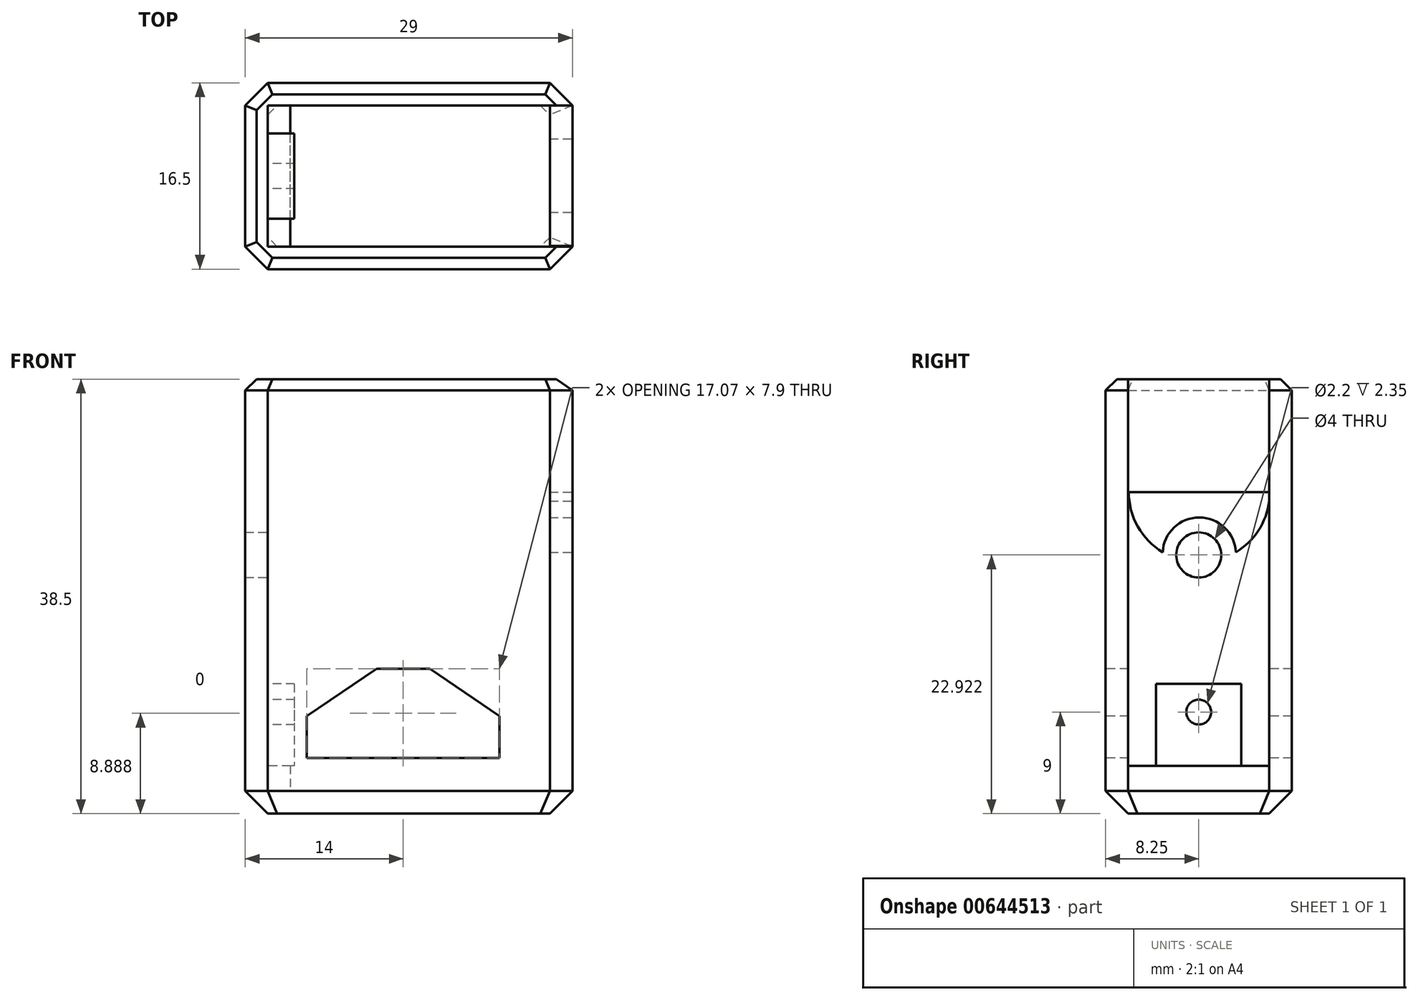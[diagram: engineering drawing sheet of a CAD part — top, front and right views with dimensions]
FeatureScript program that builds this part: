
annotation { "Feature Type Name" : "Feature", "Feature Type Description" : "" }
export const myFeature = defineFeature(function(context is Context, id is Id, definition is map)
    precondition{}
    {
        {
            var Q0;
            Q0=qCreatedBy(makeId("Top.planeOp"),FACE);
            var sketch = newSketch(context, id + "F0", { "sketchPlane" : qUnion([Q0])});
            skLineSegment(sketch, "E0.bottom", {"start": v(0, 0) * mm, "end": v(29, 0) * mm});
            skLineSegment(sketch, "E0.top", {"start": v(0, 16.5) * mm, "end": v(29, 16.5) * mm});
            skLineSegment(sketch, "E0.left", {"start": v(0, 0) * mm, "end": v(0, 16.5) * mm});
            skLineSegment(sketch, "E0.right", {"start": v(29, 0) * mm, "end": v(29, 16.5) * mm});
            skSolve(sketch);
        }
        {
            var Q0;
            Q0=makeQuery(id+"F0.imprint","IMPRINT",FACE,{"disambiguationData":[TD([[makeQuery(id+"F0.imprint","IMPRINT",EDGE,{"derivedFrom":sQuery(id+"F0.wireOp",EDGE,"E0.bottom")}),1.0]])]});
            extrude(context, id + "F1", {"entities" : qUnion([Q0]), "depth" : 38.5 * mm, "offsetDistance" : 25 * mm});
        }
        {
            var Q0;
            Q0=makeQuery(id+"F1.opExtrude","SWEPT_EDGE",EDGE,{"disambiguationData":[OSD([sQuery(id+"F0.wireOp",EDGE,"E0.bottom"),sQuery(id+"F0.wireOp",EDGE,"E0.left")])]});
            var Q1;
            Q1=makeQuery(id+"F1.opExtrude","SWEPT_EDGE",EDGE,{"disambiguationData":[OSD([sQuery(id+"F0.wireOp",EDGE,"E0.top"),sQuery(id+"F0.wireOp",EDGE,"E0.left")])]});
            var Q2;
            Q2=makeQuery(id+"F1.opExtrude","SWEPT_EDGE",EDGE,{"disambiguationData":[OSD([sQuery(id+"F0.wireOp",EDGE,"E0.bottom"),sQuery(id+"F0.wireOp",EDGE,"E0.right")])]});
            var Q3;
            Q3=makeQuery(id+"F1.opExtrude","SWEPT_EDGE",EDGE,{"disambiguationData":[OSD([sQuery(id+"F0.wireOp",EDGE,"E0.top"),sQuery(id+"F0.wireOp",EDGE,"E0.right")])]});
            chamfer(context, id + "F2", {"entities" : qUnion([Q0, Q1, Q2, Q3]), "width" : 2 * mm, "tangentPropagation" : true});
        }
        {
            var Q0;
            Q0=makeQuery(id+"F1.opExtrude","CAP_FACE",FACE,{"disambiguationData":[OSD([sQuery(id+"F0.wireOp",EDGE,"E0.bottom"),sQuery(id+"F0.wireOp",EDGE,"E0.top"),sQuery(id+"F0.wireOp",EDGE,"E0.left"),sQuery(id+"F0.wireOp",EDGE,"E0.right")])],"isStart":true});
            chamfer(context, id + "F3", {"entities" : qUnion([Q0]), "width" : 2 * mm, "tangentPropagation" : true});
        }
        {
            var Q0;
            Q0=makeQuery(id+"F1.opExtrude","CAP_FACE",FACE,{"disambiguationData":[OSD([sQuery(id+"F0.wireOp",EDGE,"E0.bottom"),sQuery(id+"F0.wireOp",EDGE,"E0.top"),sQuery(id+"F0.wireOp",EDGE,"E0.left"),sQuery(id+"F0.wireOp",EDGE,"E0.right")])],"isStart":false});
            chamfer(context, id + "F4", {"entities" : qUnion([Q0]), "width" : 1 * mm, "tangentPropagation" : true});
        }
        {
            var Q0;
            Q0=makeQuery(id+"F1.opExtrude","CAP_FACE",FACE,{"disambiguationData":[OSD([sQuery(id+"F0.wireOp",EDGE,"E0.bottom"),sQuery(id+"F0.wireOp",EDGE,"E0.top"),sQuery(id+"F0.wireOp",EDGE,"E0.left"),sQuery(id+"F0.wireOp",EDGE,"E0.right")])],"isStart":false});
            var sketch = newSketch(context, id + "F5", { "sketchPlane" : qUnion([Q0])});
            skLineSegment(sketch, "E1.bottom", {"start": v(2, 2) * mm, "end": v(27, 2) * mm});
            skLineSegment(sketch, "E1.top", {"start": v(2, 14.5) * mm, "end": v(27, 14.5) * mm});
            skLineSegment(sketch, "E1.left", {"start": v(2, 2) * mm, "end": v(2, 14.5) * mm});
            skLineSegment(sketch, "E1.right", {"start": v(27, 2) * mm, "end": v(27, 14.5) * mm});
            skSolve(sketch);
        }
        {
            var Q0;
            Q0=makeQuery(id+"F5.imprint","IMPRINT",FACE,{"disambiguationData":[TD([[makeQuery(id+"F5.imprint","IMPRINT",EDGE,{"derivedFrom":sQuery(id+"F5.wireOp",EDGE,"E1.bottom")}),1.0]])]});
            extrude(context, id + "F6", {"entities" : qUnion([Q0]), "operationType" : NewBodyOperationType.REMOVE, "oppositeDirection" : true, "depth" : 34.25 * mm, "offsetDistance" : 25 * mm});
        }
        {
            var Q0;
            Q0=makeQuery(id+"F1.opExtrude","SWEPT_FACE",FACE,{"disambiguationData":[OSD([sQuery(id+"F0.wireOp",EDGE,"E0.bottom")])]});
            var sketch = newSketch(context, id + "F7", { "sketchPlane" : qUnion([Q0])});
            skLineSegment(sketch, "E2", {"start": v(5.46, 4.94) * mm, "end": v(22.54, 4.94) * mm});
            skLineSegment(sketch, "E3", {"start": v(22.54, 4.94) * mm, "end": v(22.54, 8.66) * mm});
            skLineSegment(sketch, "E4", {"start": v(22.54, 8.66) * mm, "end": v(16.36, 12.84) * mm});
            skLineSegment(sketch, "E5", {"start": v(16.36, 12.84) * mm, "end": v(11.64, 12.84) * mm});
            skLineSegment(sketch, "E6", {"start": v(11.64, 12.84) * mm, "end": v(5.46, 8.66) * mm});
            skLineSegment(sketch, "E7", {"start": v(5.46, 8.66) * mm, "end": v(5.46, 4.94) * mm});
            skSolve(sketch);
        }
        {
            var Q0;
            Q0=makeQuery(id+"F7.imprint","IMPRINT",FACE,{"disambiguationData":[TD([[makeQuery(id+"F7.imprint","IMPRINT",EDGE,{"derivedFrom":sQuery(id+"F7.wireOp",EDGE,"E2")}),1.0]])]});
            extrude(context, id + "F8", {"entities" : qUnion([Q0]), "operationType" : NewBodyOperationType.REMOVE, "endBound" : BoundingType.THROUGH_ALL, "oppositeDirection" : true, "depth" : 25 * mm, "offsetDistance" : 25 * mm});
        }
        {
            var Q0;
            Q0=makeQuery(id+"F1.opExtrude","SWEPT_FACE",FACE,{"disambiguationData":[OSD([sQuery(id+"F0.wireOp",EDGE,"E0.right")])]});
            var sketch = newSketch(context, id + "F9", { "sketchPlane" : qUnion([Q0])});
            skCircle(sketch, "E8", {"center": v(8.3, 23) * mm, "radius": 3.25 * mm});
            skCircle(sketch, "E9", {"center": v(8.3, 28.5) * mm, "radius": 6.25 * mm});
            skLineSegment(sketch, "E10.bottom", {"start": v(2, 38.5) * mm, "end": v(14.5, 38.5) * mm});
            skLineSegment(sketch, "E10.top", {"start": v(2, 28.5) * mm, "end": v(14.5, 28.5) * mm});
            skLineSegment(sketch, "E10.left", {"start": v(2, 38.5) * mm, "end": v(2, 28.5) * mm});
            skLineSegment(sketch, "E10.right", {"start": v(14.5, 38.5) * mm, "end": v(14.5, 28.5) * mm});
            skSolve(sketch);
        }
        {
            var Q0;
            {var subQ0=sQuery(id+"F9.wireOp",EDGE,"E10.bottom");Q0=makeQuery(id+"F9.imprint","IMPRINT",FACE,{"disambiguationData":[TD([[makeQuery(id+"F9.imprint","IMPRINT",EDGE,{"derivedFrom":subQ0}),-1.0]])]});}
            var Q1;
            {var subQ1=sQuery(id+"F0.wireOp",EDGE,"E0.right");var subQ2=makeQuery(id+"F1.opExtrude","SWEPT_FACE",FACE,{"disambiguationData":[OSD([subQ1])]});var subQ3=makeQuery(id+"F4.opChamfer","BLEND_EDGE",EDGE,{"blendedFrom":[makeQuery(id+"F1.opExtrude","CAP_EDGE",EDGE,{"disambiguationData":[OSD([subQ1])],"isStart":false}),subQ2],"blendedInto":[subQ2]});Q1=makeQuery(id+"F9.imprint","IMPRINT",FACE,{"disambiguationData":[TD([[makeQuery(id+"F9.imprint","IMPRINT",EDGE,{"derivedFrom":subQ3}),1.0]])]});}
            var Q2;
            {var subQ0=sQuery(id+"F9.wireOp",EDGE,"E10.right");var subQ1=sQuery(id+"F9.wireOp",EDGE,"E9");var subQ2=makeQuery(id+"F9.imprint","INTERSECT",VERTEX,{"derivedFrom":[subQ1,subQ0]});Q2=makeQuery(id+"F9.imprint","IMPRINT",FACE,{"disambiguationData":[TD([[makeQuery(id+"F9.imprint","IMPRINT",EDGE,{"disambiguationData":[TD([[subQ2,-1.0]])],"derivedFrom":subQ1}),1.0]])]});}
            var Q3;
            {var subQ4=sQuery(id+"F9.wireOp",EDGE,"E9");var subQ6=sQuery(id+"F9.wireOp",EDGE,"E8");var subQ7=makeQuery(id+"F9.imprint","INTERSECT",VERTEX,{"disambiguationData":[OD(0.0)],"derivedFrom":[subQ6,subQ4]});Q3=makeQuery(id+"F9.imprint","IMPRINT",FACE,{"disambiguationData":[TD([[makeQuery(id+"F9.imprint","IMPRINT",EDGE,{"disambiguationData":[TD([[subQ7,1.0]])],"derivedFrom":subQ6}),-1.0]])]});}
            var Q4;
            {var subQ0=sQuery(id+"F9.wireOp",EDGE,"E9");var subQ1=sQuery(id+"F9.wireOp",EDGE,"E8");var subQ2=makeQuery(id+"F9.imprint","INTERSECT",VERTEX,{"disambiguationData":[OD(0.0)],"derivedFrom":[subQ1,subQ0]});Q4=makeQuery(id+"F9.imprint","IMPRINT",FACE,{"disambiguationData":[TD([[makeQuery(id+"F9.imprint","IMPRINT",EDGE,{"disambiguationData":[TD([[subQ2,1.0]])],"derivedFrom":subQ1}),1.0]])]});}
            var Q5;
            {var subQ0=sQuery(id+"F9.wireOp",EDGE,"E9");var subQ1=sQuery(id+"F9.wireOp",EDGE,"E8");var subQ2=makeQuery(id+"F9.imprint","INTERSECT",VERTEX,{"disambiguationData":[OD(0.0)],"derivedFrom":[subQ1,subQ0]});Q5=makeQuery(id+"F9.imprint","IMPRINT",FACE,{"disambiguationData":[TD([[makeQuery(id+"F9.imprint","IMPRINT",EDGE,{"disambiguationData":[TD([[subQ2,-1.0]])],"derivedFrom":subQ1}),1.0]])]});}
            extrude(context, id + "F10", {"entities" : qUnion([Q0, Q1, Q2, Q3, Q4, Q5]), "operationType" : NewBodyOperationType.REMOVE, "oppositeDirection" : true, "depth" : 25 * mm, "offsetDistance" : 25 * mm});
        }
        {
            var Q0;
            Q0=makeQuery(id+"F1.opExtrude","SWEPT_FACE",FACE,{"disambiguationData":[OSD([sQuery(id+"F0.wireOp",EDGE,"E0.left")])]});
            var sketch = newSketch(context, id + "F11", { "sketchPlane" : qUnion([Q0])});
            skLineSegment(sketch, "E11.bottom", {"start": v(-12.02, 11.5) * mm, "end": v(-4.48, 11.5) * mm});
            skLineSegment(sketch, "E11.top", {"start": v(-12.02, 4.25) * mm, "end": v(-4.48, 4.25) * mm});
            skLineSegment(sketch, "E11.left", {"start": v(-12.02, 11.5) * mm, "end": v(-12.02, 4.25) * mm});
            skLineSegment(sketch, "E11.right", {"start": v(-4.48, 11.5) * mm, "end": v(-4.48, 4.25) * mm});
            skCircle(sketch, "E12", {"center": v(-8.25, 9) * mm, "radius": 1.1 * mm});
            skSolve(sketch);
        }
        {
            var Q0;
            Q0 = qSketchRegion(id + "F11", true);
            extrude(context, id + "F12", {"entities" : qUnion([Q0]), "operationType" : NewBodyOperationType.ADD, "oppositeDirection" : true, "depth" : 4.35 * mm, "offsetDistance" : 25 * mm});
        }
        {
            var Q0;
            {var subQ1=sQuery(id+"F5.wireOp",EDGE,"E1.left");var subQ2=sQuery(id+"F5.wireOp",EDGE,"E1.bottom");Q0=makeQuery(id+"F12.boolean.opBoolean","SPLIT",FACE,{"disambiguationData":[TD([makeQuery(id+"F6.boolean.opBoolean","COPY",FACE,{"derivedFrom":makeQuery(id+"F6.opExtrude","SWEPT_FACE",FACE,{"disambiguationData":[OSD([subQ2])]})})])],"derivedFrom":makeQuery(id+"F6.boolean.opBoolean","COPY",FACE,{"derivedFrom":makeQuery(id+"F6.opExtrude","SWEPT_FACE",FACE,{"disambiguationData":[OSD([subQ1])]})})});}
            var sketch = newSketch(context, id + "F13", { "sketchPlane" : qUnion([Q0])});
            skCircle(sketch, "E13", {"center": v(8.25, 22.92) * mm, "radius": 2 * mm});
            skSolve(sketch);
        }
        {
            var Q0;
            Q0=makeQuery(id+"F13.imprint","IMPRINT",FACE,{"disambiguationData":[TD([[makeQuery(id+"F13.imprint","IMPRINT",EDGE,{"derivedFrom":sQuery(id+"F13.wireOp",EDGE,"E13")}),1.0]])]});
            extrude(context, id + "F14", {"entities" : qUnion([Q0]), "operationType" : NewBodyOperationType.REMOVE, "oppositeDirection" : true, "depth" : 25 * mm, "offsetDistance" : 25 * mm});
        }
        {
            var Q0;
            Q0=makeQuery(id+"F1.opExtrude","SWEPT_FACE",FACE,{"disambiguationData":[OSD([sQuery(id+"F0.wireOp",EDGE,"E0.right")])]});
            var sketch = newSketch(context, id + "F15", { "sketchPlane" : qUnion([Q0])});
            skLineSegment(sketch, "E14.bottom", {"start": v(5.48, 10.8) * mm, "end": v(11.02, 10.8) * mm});
            skLineSegment(sketch, "E14.top", {"start": v(5.48, 5.27) * mm, "end": v(11.02, 5.27) * mm});
            skLineSegment(sketch, "E14.left", {"start": v(5.48, 10.8) * mm, "end": v(5.48, 5.27) * mm});
            skLineSegment(sketch, "E14.right", {"start": v(11.02, 10.8) * mm, "end": v(11.02, 5.27) * mm});
            skSolve(sketch);
        }
        {
            var Q0;
            Q0=makeQuery(id+"F15.imprint","IMPRINT",FACE,{"disambiguationData":[TD([[makeQuery(id+"F15.imprint","IMPRINT",EDGE,{"derivedFrom":sQuery(id+"F15.wireOp",EDGE,"E14.bottom")}),-1.0]])]});
            cPlane(context, id + "F16", {"entities" : qUnion([Q0]), "cplaneType" : CPlaneType.OFFSET, "offset" : 4.45 * mm, "oppositeDirection" : true, "width" : 150 * mm, "height" : 150 * mm});
        }
        {
            var Q0;
            Q0=qCreatedBy(id+"F16.planeOp",FACE);
            var sketch = newSketch(context, id + "F17", { "sketchPlane" : qUnion([Q0])});
            skLineSegment(sketch, "E15.bottom", {"start": v(5.48, 10.76) * mm, "end": v(11.02, 10.76) * mm});
            skLineSegment(sketch, "E15.top", {"start": v(5.48, 6.22) * mm, "end": v(11.02, 6.22) * mm});
            skLineSegment(sketch, "E15.left", {"start": v(5.48, 10.76) * mm, "end": v(5.48, 6.22) * mm});
            skLineSegment(sketch, "E15.right", {"start": v(11.02, 10.76) * mm, "end": v(11.02, 6.22) * mm});
            skSolve(sketch);
        }
        {
            var Q1;
            Q1 = qSketchRegion(id + "F15", true);
            var Q2;
            Q2 = qSketchRegion(id + "F17", true);
            loft(context, id + "F18", {"operationType" : NewBodyOperationType.REMOVE, "sheetProfilesArray" : [{ "sheetProfileEntities" : qUnion([Q1]) }, { "sheetProfileEntities" : qUnion([Q2]) }]});
        }
    });
